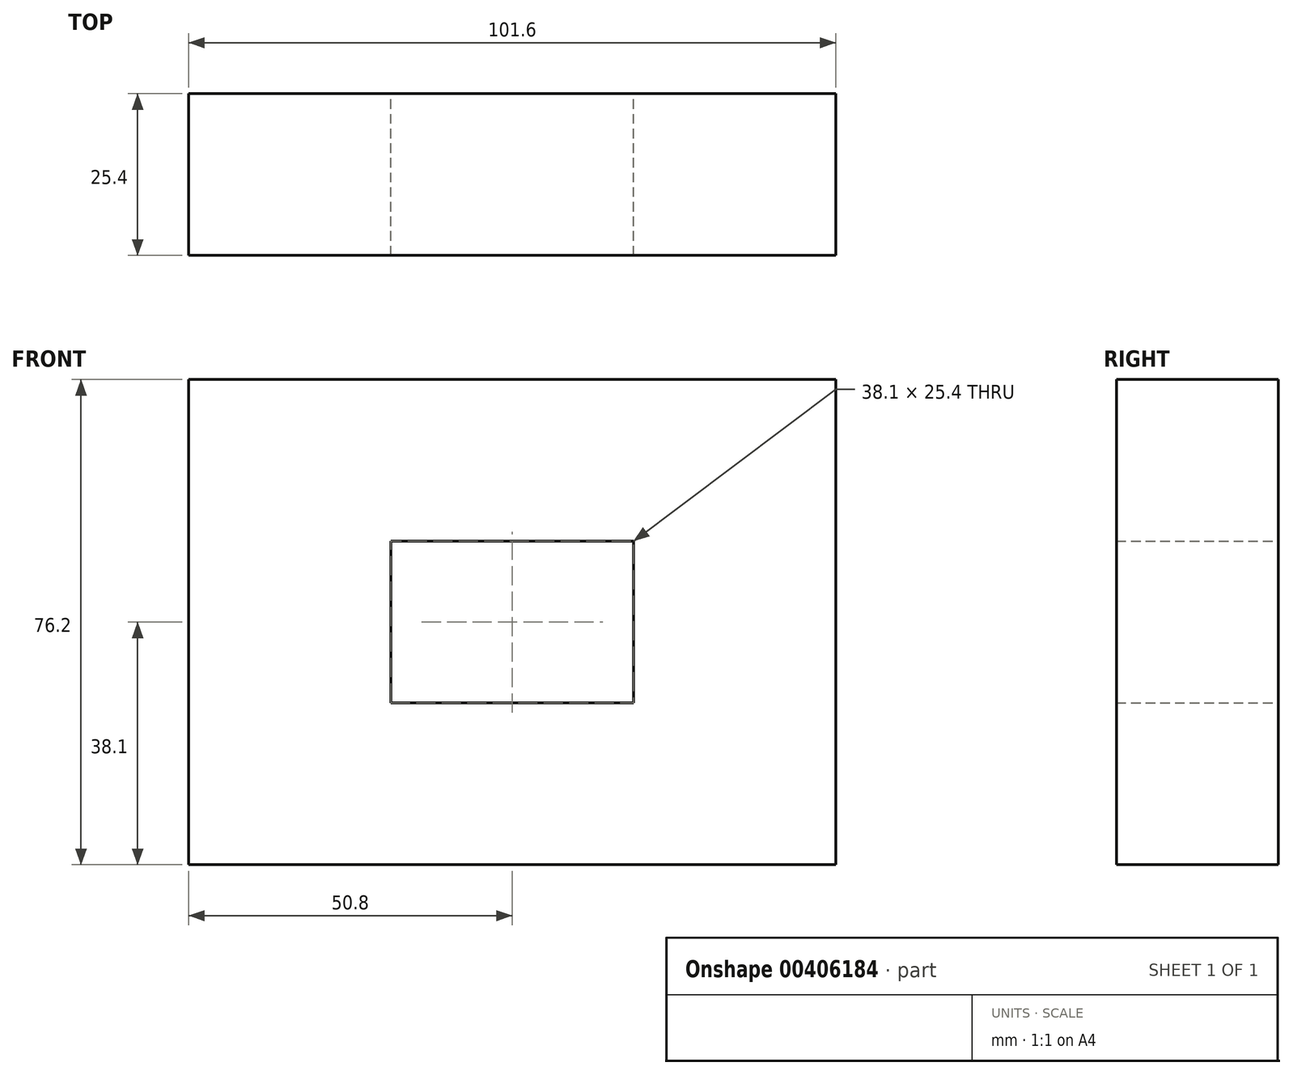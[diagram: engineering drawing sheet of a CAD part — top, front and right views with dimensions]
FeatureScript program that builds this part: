
annotation { "Feature Type Name" : "Feature", "Feature Type Description" : "" }
export const myFeature = defineFeature(function(context is Context, id is Id, definition is map)
    precondition{}
    {
        {
            var Q0;
            Q0=qCreatedBy(makeId("Front.planeOp"),FACE);
            var sketch = newSketch(context, id + "F0", { "sketchPlane" : qUnion([Q0])});
            skLineSegment(sketch, "E0.bottom", {"start": v(-50.8, 38.1) * mm, "end": v(50.8, 38.1) * mm});
            skLineSegment(sketch, "E0.top", {"start": v(-50.8, -38.1) * mm, "end": v(50.8, -38.1) * mm});
            skLineSegment(sketch, "E0.left", {"start": v(-50.8, 38.1) * mm, "end": v(-50.8, -38.1) * mm});
            skLineSegment(sketch, "E0.right", {"start": v(50.8, 38.1) * mm, "end": v(50.8, -38.1) * mm});
            skPoint(sketch, "E0.middle", {"position": v(0, 0) * mm});
            skLineSegment(sketch, "E1.bottom", {"start": v(-19.05, 12.7) * mm, "end": v(19.05, 12.7) * mm});
            skLineSegment(sketch, "E1.top", {"start": v(-19.05, -12.7) * mm, "end": v(19.05, -12.7) * mm});
            skLineSegment(sketch, "E1.left", {"start": v(-19.05, 12.7) * mm, "end": v(-19.05, -12.7) * mm});
            skLineSegment(sketch, "E1.right", {"start": v(19.05, 12.7) * mm, "end": v(19.05, -12.7) * mm});
            skSolve(sketch);
        }
        {
            var Q0;
            Q0 = qSketchRegion(id + "F0", true);
            extrude(context, id + "F1", {"entities" : qUnion([Q0]), "endBound" : BoundingType.SYMMETRIC, "depth" : 25.4 * mm});
        }
    });
